# Revit family: XTe - Cuerpo de marca de alzado
name_source: partatom
category: Marcas de alzado
revit_build: Autodesk Revit 2013 (Build: 20121003_2115(x64)
units: mm (PartAtom-declared; Revit-internal decimal feet)

## types (7) — shared parameters

## per-type parameters (varying)
| type | Tipo |
| Flecha y Datos con relleno | XTe - Puntero de marca de alzado : Flecha y Datos con relleno |
| Flecha y Número de Plano sin relleno | XTe - Puntero de marca de alzado : Flecha y Número de Plano sin relleno |
| Flecha y Nombre | XTe - Puntero de marca de alzado : Flecha y Nombre de Vista con relleno |
| Flecha y Datos sin relleno | XTe - Puntero de marca de alzado : Flecha y Datos sin relleno |
| Flecha y Número de Plano con relleno | XTe - Puntero de marca de alzado : Flecha y Número de Plano con relleno |
| Flecha con relleno | XTe - Puntero de marca de alzado : Flecha sin Datos con relleno |
| Flecha sin relleno | XTe - Puntero de marca de alzado : Flecha sin Datos sin relleno |

## geometry (parser evidence)
native form markers: Blend x7
no freeform markers — native parametric forms only
